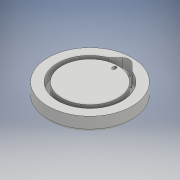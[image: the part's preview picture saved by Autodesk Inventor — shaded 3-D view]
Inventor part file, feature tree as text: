
AUTODESK INVENTOR PART (.ipt)
format: ipt  version: 2018.3 (Build 223284000, 284)  size: 351,744 bytes
history: native  units: mm
features: sketch x6, extrude x5, plane x5, projected_geometry x4, fillet x3, revolve x2, other x1
ambient origin geometry x8: Origin, YZ Plane, XZ Plane, XY Plane, X Axis, Y Axis, Z Axis, Center Point
bodies: Solid1 (feature_tree)
feature tree (26):
  extrude  "Extrusion1"  Depth=25.0mm TaperAngle=0.0deg
  extrude  "Extrusion2"  Depth=20.0mm TaperAngle=0.0deg
  extrude  "Extrusion4"  Depth=17.5mm
  fillet  "Fillet1"  [1 undecoded]
  plane  "Work Plane1"
  other  "Work Axis1"
  plane  "Work Plane9"
  plane  "Work Plane10"
  extrude  "Extrusion10"  Depth=5.0mm
  revolve  "Revolution3"  Angle=90.0deg
  fillet  "Fillet3"  [1 undecoded]
  extrude  "Extrusion13"  Depth=1.0mm TaperAngle=0.0deg
  fillet  "Fillet5"  [1 undecoded]
  revolve  "Revolution5"  [1 undecoded]
  sketch  "Sketch1"  dims[d0=150.0mm d1=25.0mm d2=0.0mm]
  sketch  "Sketch2"  dims[d4=116.0mm d5=20.0mm d6=0.0mm]
  sketch  "Sketch3"  dims[d12=25.0mm d13=17.5mm d15=45.0deg]
  plane  "Work Plane2"
  plane  "Work Plane3"
  sketch  "Sketch13"  dims[d16=5.0mm d17=0.0mm d24=5.0mm]
  sketch  "Sketch16"  dims[d25=0.0mm d29=90.0deg d30=90.0deg]
  projected_geometry  "Projected Loop8"
  projected_geometry  "Projected Loop9"
  sketch  "Sketch18"  dims[d60=8.0mm d61=20.0mm d62=0.0mm d69=180.0deg d70=10.0mm d72=58.0mm d74=4.0mm d76=5.75mm d77=10.0mm d78=17.0mm d79=0.0mm d80=17.0mm d81=1.0mm d82=90.0deg]
  projected_geometry  "Projected Loop10"
  projected_geometry  "Projected Loop11"
note: 4 required parameter values undecoded (feature->parameter linkage not recoverable at this tier; creation-order binding heuristic only, values carry confidence <= 0.55)